# Revit family: KS Husky, Typ IV-19, M10-M12, Ø133-219,1
name_source: partatom
category: HLS-Bauteile
revit_build: Autodesk Revit 2017 (Build: 20190507_1515(x64)
units: mm (PartAtom-declared; Revit-internal decimal feet)

## family parameters
Arbeitsebenenbasiert = Ja
Beim Laden mit Abzugskörper schneiden = Nein
Bemaßung runder Anschluss = Durchmesser verwenden
Gemeinsam genutzt = Ja
Immer vertikal = Nein
Raumberechnungspunkt = Nein
Teiletyp = Normal

## types (5) — shared parameters
Anschluss = M10/M12
Baustoffklasse = B2
DVS = 18 mm  [stored 0.0590551 ft]
Dichte Kern = 120 kg/m³
Dämmkörper = KA/PU
Fabrikat = MEFA
Firma = MEFA Befestigungs- und Montagesysteme GmbH
HGA = 22 mm  [stored 0.0721785 ft]
Kurztext1 = Kälteschelle Husky IV 19
L = 51 mm  [stored 0.167323 ft]
MB = 35 mm  [stored 0.114829 ft]
MD = 4 mm  [stored 0.0131234 ft]
Material = Stahl
Material Mantel = Kunststoff
Materialname = S235
Mengeneinheit = St
Oberflaeche = galvanisch verzinkt
Rohrschellentyp = Maxima PSM
Schalenlänge = 51 mm
Typ = IV 19
Vorgabe-Ansicht = 1219 mm
Wasserdampfdiffusionswiderstand = 7000 µ
Wärmeleitfähigkeit = 0.029 W/mK
max. Temperaturbeständigkeit = 105 °C
mittl. Nenndruckfestigkeit Kern = 1,35 N/mm²
stat. Belastung Kern = 0,27 N/mm²

## per-type parameters (varying)
- Kälteschelle Husky, Typ IV-19, M10/M12, Ø133: A=55 mm  [stored 0.180446 ft]; AB=1 mm  [stored 0.00328084 ft]; Anschlußhöhe=54 mm; Artikelnummer=6841330; B=265 mm; Breite=265 mm; D=133 mm  [stored 0.436352 ft]; D0=191 mm  [stored 0.62664 ft]; DF1=32 mm  [stored 0.104987 ft]; DF2=32 mm  [stored 0.104987 ft]; DS=29 mm  [stored 0.0951444 ft]; Dmax=135 mm  [stored 0.442913 ft]; Dmin=132 mm  [stored 0.433071 ft]; Dämmstärke=29 mm  [stored 0.0951444 ft]; EAN=4250928440891; Gewicht=1.03 kg; Gewicht pro Bauteil=1.03 kg; H=221 mm  [stored 0.725066 ft]; Kurztext2=133 mm Iso 29 x 51 mm M10/M12; R=96 mm; RM=100 mm  [stored 0.328084 ft]; Rohraußendurchmesser Stahl=133 mm; S=233 mm; max. zul. Last=1.69 kN; vpe=4 St
- Kälteschelle Husky, Typ IV-19, M10/M12, Ø139,7: A=52 mm; AB=2 mm  [stored 0.00656168 ft]; Anschlußhöhe=51 mm; Artikelnummer=6841400; B=265 mm; Breite=265 mm; D=140 mm  [stored 0.459318 ft]; D0=191 mm  [stored 0.62664 ft]; DF1=33 mm  [stored 0.108268 ft]; DF2=33 mm  [stored 0.108268 ft]; DS=26 mm; Dmax=140 mm  [stored 0.459318 ft]; Dmin=138 mm  [stored 0.452756 ft]; Dämmstärke=26 mm; EAN=4250928440907; Gewicht=1.02 kg; Gewicht pro Bauteil=1.02 kg; H=221 mm  [stored 0.725066 ft]; Kurztext2=139,7 mm Iso 26 x 51 mm M10/M12; R=96 mm; RM=100 mm  [stored 0.328084 ft]; Rohraußendurchmesser Stahl=139,7 mm; S=232 mm; max. zul. Last=1.78 kN; vpe=4 St
- Kälteschelle Husky, Typ IV-19, M10/M12, Ø160: A=52 mm; AB=2 mm  [stored 0.00656168 ft]; Anschlußhöhe=51 mm; Artikelnummer=6841600; B=287 mm; Breite=265 mm; D=160 mm  [stored 0.524934 ft]; D0=212 mm  [stored 0.695538 ft]; DF1=33 mm  [stored 0.108268 ft]; DF2=33 mm  [stored 0.108268 ft]; DS=26 mm; Dmax=161 mm  [stored 0.528215 ft]; Dmin=158 mm; Dämmstärke=26 mm; EAN=4250928440907; Gewicht=1.02 kg; Gewicht pro Bauteil=1.02 kg; H=242 mm  [stored 0.793963 ft]; Kurztext2=139,7 mm Iso 26 x 51 mm M10/M12; R=106 mm  [stored 0.347769 ft]; RM=110 mm  [stored 0.360892 ft]; Rohraußendurchmesser Stahl=139,7 mm; S=254 mm; max. zul. Last=1.78 kN; vpe=4 St
- Kälteschelle Husky, Typ IV-19, M10/M12, Ø168,3: A=52 mm; AB=1 mm  [stored 0.00328084 ft]; Anschlußhöhe=51 mm; Artikelnummer=6841680; B=297 mm; Breite=297 mm; D=168 mm; D0=221 mm  [stored 0.725066 ft]; DF1=33 mm  [stored 0.108268 ft]; DF2=33 mm  [stored 0.108268 ft]; DS=26 mm; Dmax=170 mm  [stored 0.557743 ft]; Dmin=167 mm  [stored 0.5479 ft]; Dämmstärke=26 mm; EAN=4250928440921; Gewicht=1.15 kg; Gewicht pro Bauteil=1.15 kg; H=251 mm; Kurztext2=168,3 mm Iso 26 x 51 mm M10/M12; R=111 mm; RM=115 mm; Rohraußendurchmesser Stahl=168,3 mm; S=264 mm; max. zul. Last=2.14 kN; vpe=2 St
- Kälteschelle Husky, Typ IV-19, M10/M12, Ø219,1: A=52 mm; AB=1 mm  [stored 0.00328084 ft]; Anschlußhöhe=51 mm; Artikelnummer=6842190; B=346 mm; Breite=346 mm; D=219 mm; D0=271 mm; DF1=33 mm  [stored 0.108268 ft]; DF2=32 mm  [stored 0.104987 ft]; DS=26 mm; Dmax=221 mm  [stored 0.725066 ft]; Dmin=218 mm  [stored 0.715223 ft]; Dämmstärke=26 mm; EAN=4250928440938; Gewicht=1.36 kg; Gewicht pro Bauteil=1.36 kg; H=301 mm; Kurztext2=219,1 mm Iso 26 x 51 mm M10/M12; R=136 mm; RM=140 mm  [stored 0.459318 ft]; Rohraußendurchmesser Stahl=219,1 mm; S=313 mm; max. zul. Last=2.68 kN; vpe=1 St

note: [stored X ft] marks values corroborated as IEEE doubles in the binary element streams (Revit-internal decimal feet)

## geometry (parser evidence)
native form markers: Sweep x6
no freeform markers — native parametric forms only
